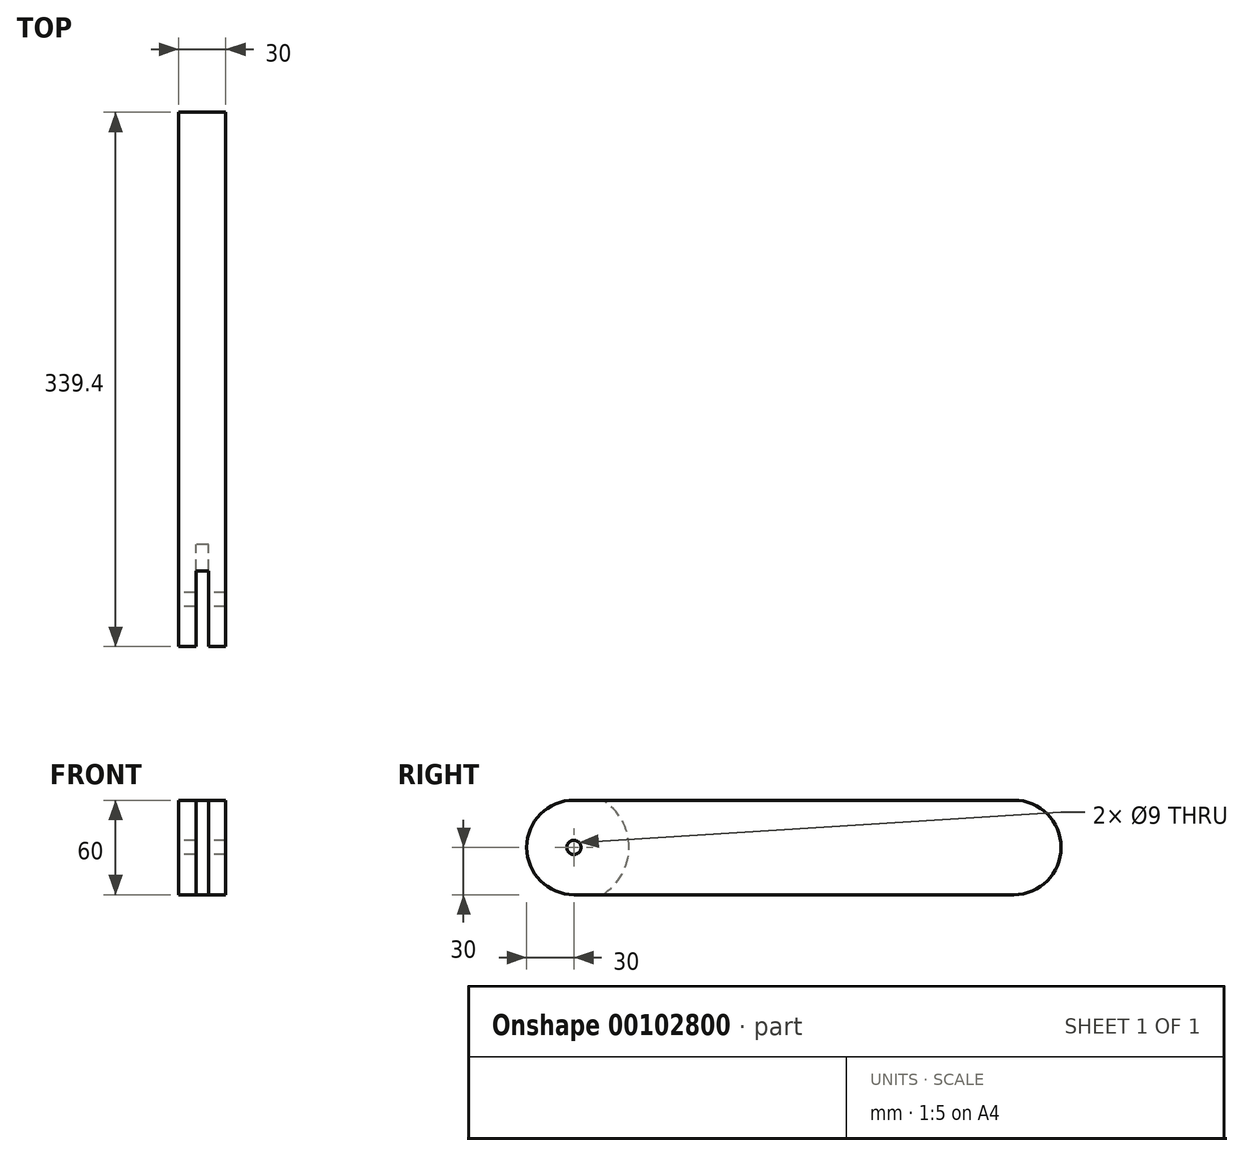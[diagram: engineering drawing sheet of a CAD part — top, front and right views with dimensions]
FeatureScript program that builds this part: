
annotation { "Feature Type Name" : "Feature", "Feature Type Description" : "" }
export const myFeature = defineFeature(function(context is Context, id is Id, definition is map)
    precondition{}
    {
        {
            var Q0;
            Q0=qCreatedBy(makeId("Right.planeOp"),FACE);
            var sketch = newSketch(context, id + "F0", { "sketchPlane" : qUnion([Q0])});
            skLineSegment(sketch, "E0.bottom", {"start": v(139.7, 30) * mm, "end": v(-139.7, 30) * mm});
            skLineSegment(sketch, "E0.top", {"start": v(139.7, -30) * mm, "end": v(-139.7, -30) * mm});
            skPoint(sketch, "E0.middle", {"position": v(0, 0) * mm});
            skArc(sketch, "E1", {"start": v(-139.7, 30) * mm, "mid": v(-169.7, 0) * mm, "end": v(-139.7, -30) * mm});
            skArc(sketch, "E2", {"start": v(139.7, 30) * mm, "mid": v(169.7, 0) * mm, "end": v(139.7, -30) * mm});
            skPoint(sketch, "E3", {"position": v(0, 30) * mm});
            skSolve(sketch);
        }
        {
            var Q0;
            Q0=makeQuery(id+"F0.imprint","IMPRINT",FACE,{"disambiguationData":[TD([[makeQuery(id+"F0.imprint","IMPRINT",EDGE,{"derivedFrom":sQuery(id+"F0.wireOp",EDGE,"E0.bottom")}),1.0]])]});
            extrude(context, id + "F1", {"entities" : qUnion([Q0]), "depth" : 30 * mm});
        }
        {
            var Q0;
            Q0=makeQuery(id+"F1.opExtrude","CAP_FACE",FACE,{"disambiguationData":[OSD([sQuery(id+"F0.wireOp",EDGE,"E0.bottom"),sQuery(id+"F0.wireOp",EDGE,"E0.top"),sQuery(id+"F0.wireOp",EDGE,"E1"),sQuery(id+"F0.wireOp",EDGE,"E2")])],"isStart":true});
            var Q1;
            Q1=makeQuery(id+"F1.opExtrude","CAP_FACE",FACE,{"disambiguationData":[OSD([sQuery(id+"F0.wireOp",EDGE,"E0.bottom"),sQuery(id+"F0.wireOp",EDGE,"E0.top"),sQuery(id+"F0.wireOp",EDGE,"E1"),sQuery(id+"F0.wireOp",EDGE,"E2")])],"isStart":false});
            cPlane(context, id + "F2", {"entities" : qUnion([Q0, Q1]), "cplaneType" : CPlaneType.MID_PLANE, "offset" : 25 * mm, "width" : 150 * mm, "height" : 150 * mm});
        }
        {
            var Q0;
            Q0=qCreatedBy(id+"F2.planeOp",FACE);
            var sketch = newSketch(context, id + "F3", { "sketchPlane" : qUnion([Q0])});
            skArc(sketch, "E4.0", {"start": v(139.7, 30) * mm, "mid": v(169.7, 0) * mm, "end": v(139.7, -30) * mm});
            skCircle(sketch, "E5", {"center": v(139.7, 0) * mm, "radius": 35 * mm});
            skSolve(sketch);
        }
        {
            var Q0;
            Q0=makeQuery(id+"F3.imprint","IMPRINT",FACE,{"disambiguationData":[TD([[makeQuery(id+"F3.imprint","IMPRINT",EDGE,{"derivedFrom":sQuery(id+"F3.wireOp",EDGE,"E5")}),1.0]])]});
            extrude(context, id + "F4", {"entities" : qUnion([Q0]), "operationType" : NewBodyOperationType.REMOVE, "endBound" : BoundingType.SYMMETRIC, "oppositeDirection" : true, "depth" : 8 * mm});
        }
        {
            var Q0;
            Q0=sQuery(id+"F0.wireOp",VERTEX,"E1.center");
            var Q1;
            Q1=makeQuery(id+"F1.opExtrude","SWEPT_BODY",BODY,{"disambiguationData":[OSD([sQuery(id+"F0.wireOp",EDGE,"E0.bottom"),sQuery(id+"F0.wireOp",EDGE,"E0.top"),sQuery(id+"F0.wireOp",EDGE,"E1"),sQuery(id+"F0.wireOp",EDGE,"E2")])]});
            hole(context, id + "F5", {"style" : HoleStyle.SIMPLE, "endStyle" : HoleEndStyle.THROUGH, "oppositeDirection" : true, "holeDiameter" : 9 * mm, "startFromSketch" : true, "locations" : qUnion([Q0]), "scope" : qUnion([Q1]), "isTappedThrough" : true});
        }
    });
